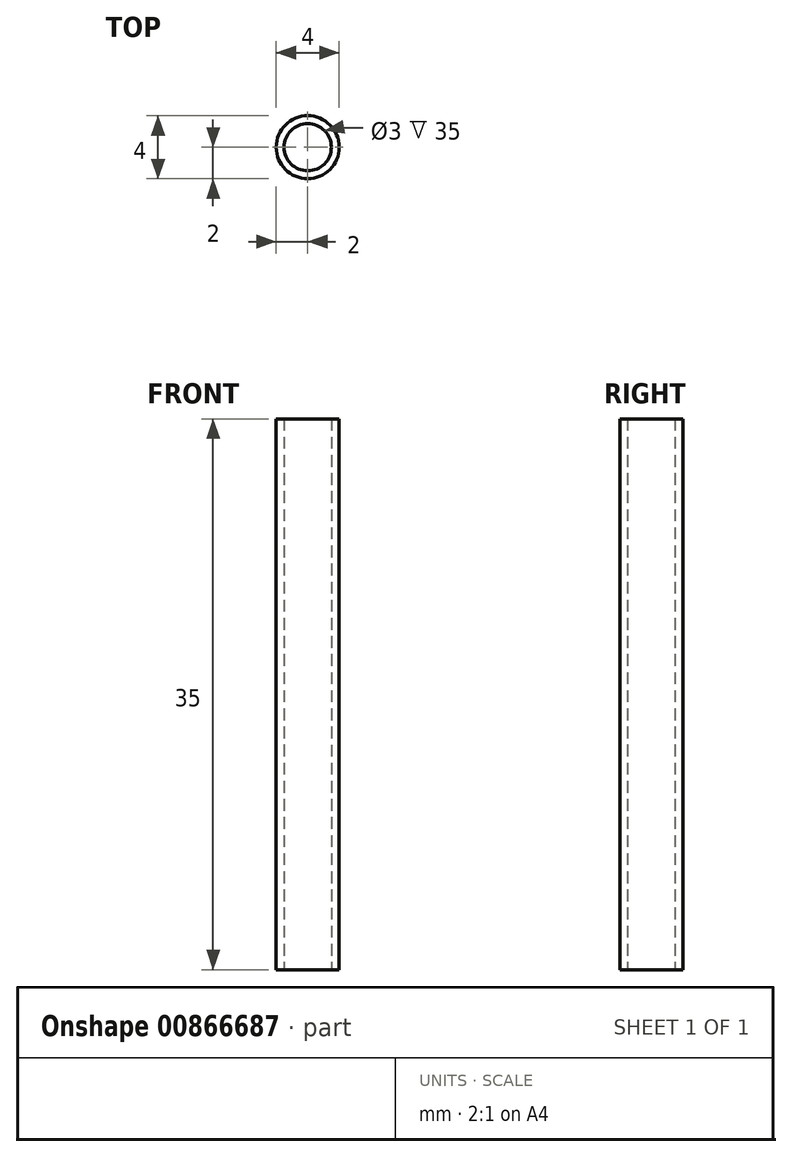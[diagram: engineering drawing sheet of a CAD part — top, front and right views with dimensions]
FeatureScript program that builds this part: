
annotation { "Feature Type Name" : "Feature", "Feature Type Description" : "" }
export const myFeature = defineFeature(function(context is Context, id is Id, definition is map)
    precondition{}
    {
        {
            var Q0;
            Q0=qCreatedBy(makeId("Top.planeOp"),FACE);
            var sketch = newSketch(context, id + "F0", { "sketchPlane" : qUnion([Q0])});
            skCircle(sketch, "E0", {"center": v(0, 0) * mm, "radius": 2 * mm});
            skCircle(sketch, "E1", {"center": v(0, 0) * mm, "radius": 1.5 * mm});
            skSolve(sketch);
        }
        {
            var Q0;
            Q0=makeQuery(id+"F0.imprint","IMPRINT",FACE,{"disambiguationData":[TD([[makeQuery(id+"F0.imprint","IMPRINT",EDGE,{"derivedFrom":sQuery(id+"F0.wireOp",EDGE,"E0")}),1.0]])]});
            extrude(context, id + "F1", {"entities" : qUnion([Q0]), "depth" : 35 * mm, "offsetDistance" : 25.4 * mm});
        }
    });
